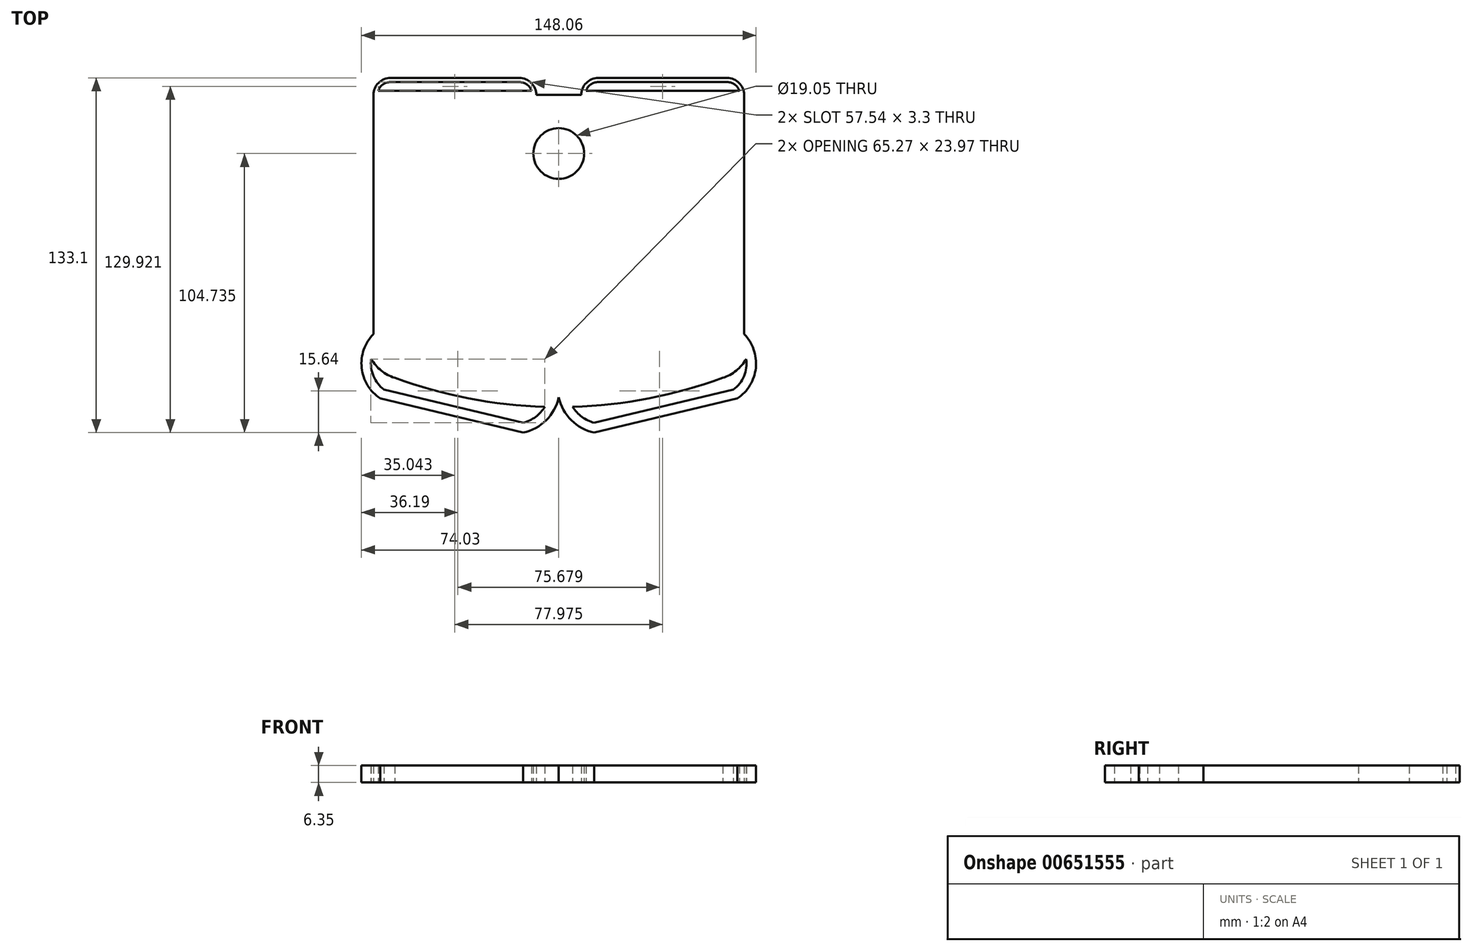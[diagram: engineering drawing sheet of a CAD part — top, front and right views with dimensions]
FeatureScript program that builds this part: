
annotation { "Feature Type Name" : "Feature", "Feature Type Description" : "" }
export const myFeature = defineFeature(function(context is Context, id is Id, definition is map)
    precondition{}
    {
        {
            var Q0;
            Q0=qCreatedBy(makeId("Top.planeOp"),FACE);
            var sketch = newSketch(context, id + "F0", { "sketchPlane" : qUnion([Q0])});
            skLineSegment(sketch, "E0", {"start": v(-8.45, 62.54) * mm, "end": v(8.45, 62.54) * mm});
            skPoint(sketch, "E1", {"position": v(0, -51.05) * mm});
            skLineSegment(sketch, "E2", {"start": v(-69.53, 51.1) * mm, "end": v(-69.53, -27.2) * mm});
            skLineSegment(sketch, "E3.MirrorCS", {"start": v(69.53, 51.1) * mm, "end": v(69.53, -27.2) * mm});
            skPoint(sketch, "E4.orphan", {"position": v(-69.53, -43.52) * mm});
            skPoint(sketch, "E5.orphan", {"position": v(69.53, -43.52) * mm});
            skPoint(sketch, "E6.visualSharp", {"position": v(-69.53, 62.54) * mm});
            skPoint(sketch, "E7.visualSharp", {"position": v(69.53, 62.54) * mm});
            skPoint(sketch, "E8.visualSharp", {"position": v(-69.53, -36.66) * mm});
            skPoint(sketch, "E9.visualSharp", {"position": v(69.53, -36.66) * mm});
            skLineSegment(sketch, "E10.top", {"start": v(-63.18, 68.89) * mm, "end": v(-14.8, 68.89) * mm});
            skLineSegment(sketch, "E10.left", {"start": v(-69.53, 51.1) * mm, "end": v(-69.53, 62.54) * mm});
            skLineSegment(sketch, "E11", {"start": v(-8.45, 62.54) * mm, "end": v(-8.45, 62.54) * mm});
            skPoint(sketch, "E12.orphan", {"position": v(0, 68.89) * mm});
            skPoint(sketch, "E13.visualSharp", {"position": v(-69.53, 68.89) * mm});
            skArc(sketch, "E13.filletArc", {"start": v(-63.18, 68.89) * mm, "mid": v(-67.67, 67.03) * mm, "end": v(-69.53, 62.54) * mm});
            skPoint(sketch, "E14.visualSharp", {"position": v(-8.45, 68.89) * mm});
            skArc(sketch, "E14.filletArc", {"start": v(-8.45, 62.54) * mm, "mid": v(-10.3, 67.03) * mm, "end": v(-14.8, 68.89) * mm});
            skArc(sketch, "E15.0", {"start": v(-63.18, 67.36) * mm, "mid": v(-66, 66.45) * mm, "end": v(-67.76, 64.06) * mm});
            skLineSegment(sketch, "E15.1", {"start": v(-63.18, 67.36) * mm, "end": v(-14.8, 67.36) * mm});
            skArc(sketch, "E15.2", {"start": v(-10.22, 64.06) * mm, "mid": v(-11.98, 66.45) * mm, "end": v(-14.8, 67.36) * mm});
            skLineSegment(sketch, "E15.3", {"start": v(-67.76, 64.06) * mm, "end": v(-10.22, 64.06) * mm});
            skArc(sketch, "E16.MirrorCS", {"start": v(8.45, 62.54) * mm, "mid": v(10.3, 67.03) * mm, "end": v(14.8, 68.89) * mm});
            skLineSegment(sketch, "E17.MirrorCS", {"start": v(63.18, 68.89) * mm, "end": v(14.8, 68.89) * mm});
            skArc(sketch, "E18.MirrorCS", {"start": v(10.22, 64.06) * mm, "mid": v(11.98, 66.45) * mm, "end": v(14.8, 67.36) * mm});
            skLineSegment(sketch, "E19.MirrorCS", {"start": v(63.18, 67.36) * mm, "end": v(14.8, 67.36) * mm});
            skLineSegment(sketch, "E20.MirrorCS", {"start": v(67.76, 64.06) * mm, "end": v(10.22, 64.06) * mm});
            skArc(sketch, "E21.MirrorCS", {"start": v(63.18, 68.89) * mm, "mid": v(67.67, 67.03) * mm, "end": v(69.53, 62.54) * mm});
            skArc(sketch, "E22.MirrorCS", {"start": v(63.18, 67.36) * mm, "mid": v(66, 66.45) * mm, "end": v(67.76, 64.06) * mm});
            skLineSegment(sketch, "E23", {"start": v(69.53, 51.1) * mm, "end": v(69.53, 62.54) * mm});
            skPoint(sketch, "E24.endSnap0", {"position": v(-67.01, -35.2) * mm});
            skLineSegment(sketch, "E25", {"start": v(-67.01, -51.42) * mm, "end": v(-13.34, -64.21) * mm});
            skArc(sketch, "E26", {"start": v(-69.53, -27.2) * mm, "mid": v(-73.94, -39.9) * mm, "end": v(-67.01, -51.42) * mm});
            skArc(sketch, "E27", {"start": v(-13.34, -64.21) * mm, "mid": v(-4.73, -59.6) * mm, "end": v(0, -51.05) * mm});
            skLineSegment(sketch, "E28.0", {"start": v(-70.36, -36.58) * mm, "end": v(-70.36, -36.58) * mm});
            skLineSegment(sketch, "E28.1", {"start": v(-65.52, -48.12) * mm, "end": v(-13.34, -60.56) * mm});
            skArc(sketch, "E28.2", {"start": v(-13.34, -60.56) * mm, "mid": v(-8.7, -58.32) * mm, "end": v(-5.2, -54.53) * mm});
            skArc(sketch, "E28.3", {"start": v(-70.36, -36.58) * mm, "mid": v(-69.52, -43.01) * mm, "end": v(-65.52, -48.12) * mm});
            skArc(sketch, "E28.4", {"start": v(-61.52, -43.68) * mm, "mid": v(-33.8, -51.38) * mm, "end": v(-5.2, -54.53) * mm});
            skArc(sketch, "E28.5", {"start": v(-70.36, -36.58) * mm, "mid": v(-66.6, -40.96) * mm, "end": v(-61.52, -43.68) * mm});
            skArc(sketch, "E29.MirrorCS", {"start": v(13.34, -64.21) * mm, "mid": v(4.73, -59.6) * mm, "end": v(0, -51.05) * mm});
            skArc(sketch, "E30.MirrorCS", {"start": v(13.34, -60.56) * mm, "mid": v(8.7, -58.32) * mm, "end": v(5.2, -54.53) * mm});
            skArc(sketch, "E31.MirrorCS", {"start": v(61.52, -43.68) * mm, "mid": v(33.8, -51.38) * mm, "end": v(5.2, -54.53) * mm});
            skLineSegment(sketch, "E32.MirrorCS", {"start": v(65.52, -48.12) * mm, "end": v(13.34, -60.56) * mm});
            skArc(sketch, "E33.MirrorCS", {"start": v(69.53, -27.2) * mm, "mid": v(73.94, -39.9) * mm, "end": v(67.01, -51.42) * mm});
            skArc(sketch, "E34.MirrorCS", {"start": v(70.36, -36.58) * mm, "mid": v(69.52, -43.01) * mm, "end": v(65.52, -48.12) * mm});
            skArc(sketch, "E35.MirrorCS", {"start": v(70.36, -36.58) * mm, "mid": v(66.6, -40.96) * mm, "end": v(61.52, -43.68) * mm});
            skLineSegment(sketch, "E36.MirrorCS", {"start": v(67.01, -51.42) * mm, "end": v(13.34, -64.21) * mm});
            skCircle(sketch, "E37", {"center": v(0, 40.53) * mm, "radius": 9.53 * mm});
            skSolve(sketch);
        }
        {
            var Q0;
            Q0=makeQuery(id+"F0.imprint","IMPRINT",FACE,{"disambiguationData":[TD([[makeQuery(id+"F0.imprint","IMPRINT",EDGE,{"derivedFrom":sQuery(id+"F0.wireOp",EDGE,"E0")}),-1.0]])]});
            extrude(context, id + "F1", {"entities" : qUnion([Q0]), "depth" : 6.35 * mm, "offsetDistance" : 25.4 * mm});
        }
    });
